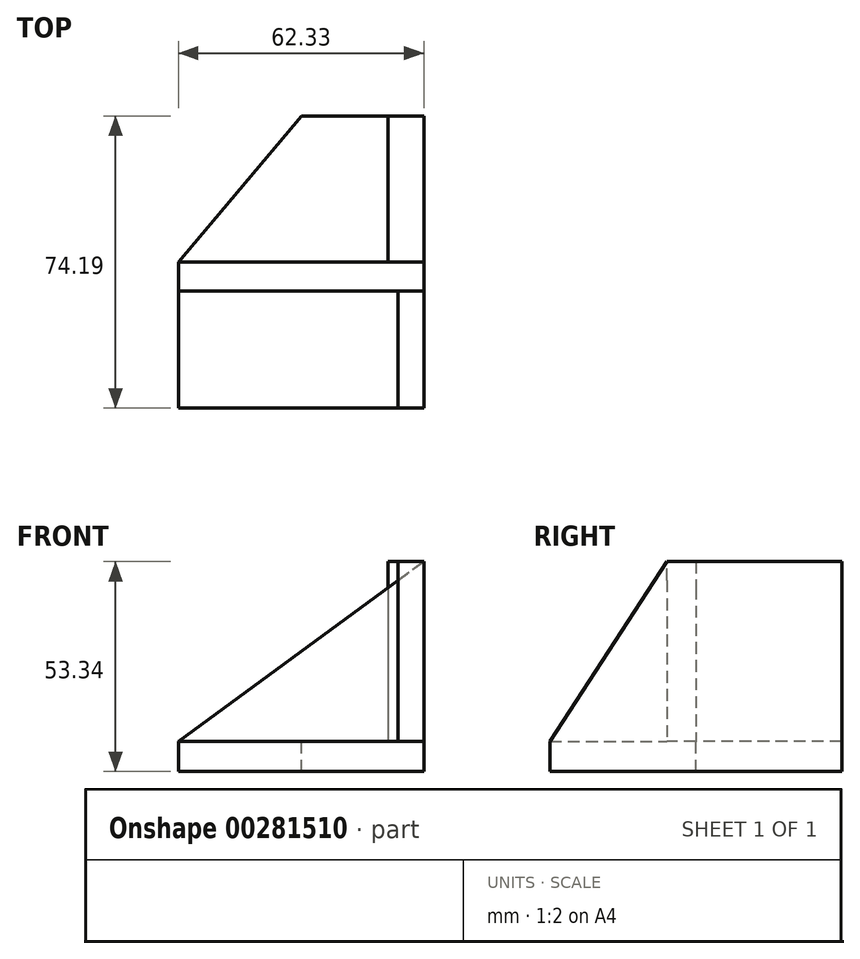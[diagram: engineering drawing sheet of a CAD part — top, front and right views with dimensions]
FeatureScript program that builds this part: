
annotation { "Feature Type Name" : "Feature", "Feature Type Description" : "" }
export const myFeature = defineFeature(function(context is Context, id is Id, definition is map)
    precondition{}
    {
        {
            var Q0;
            Q0=qCreatedBy(makeId("Top.planeOp"),FACE);
            var sketch = newSketch(context, id + "F0", { "sketchPlane" : qUnion([Q0])});
            skLineSegment(sketch, "E0.bottom", {"start": v(-31.28, 35.35) * mm, "end": v(31.05, 35.35) * mm});
            skLineSegment(sketch, "E0.top", {"start": v(-31.28, -38.84) * mm, "end": v(31.05, -38.84) * mm});
            skLineSegment(sketch, "E0.left", {"start": v(-31.28, 35.35) * mm, "end": v(-31.28, -38.84) * mm});
            skLineSegment(sketch, "E0.right", {"start": v(31.05, 35.35) * mm, "end": v(31.05, -38.84) * mm});
            skSolve(sketch);
        }
        {
            var Q0;
            Q0=makeQuery(id+"F0.imprint","IMPRINT",FACE,{"disambiguationData":[TD([[makeQuery(id+"F0.imprint","IMPRINT",EDGE,{"derivedFrom":sQuery(id+"F0.wireOp",EDGE,"E0.bottom")}),-1.0]])]});
            extrude(context, id + "F1", {"entities" : qUnion([Q0]), "depth" : 7.62 * mm});
        }
        {
            var Q0;
            Q0=makeQuery(id+"F1.opExtrude","CAP_FACE",FACE,{"disambiguationData":[OSD([sQuery(id+"F0.wireOp",EDGE,"E0.bottom"),sQuery(id+"F0.wireOp",EDGE,"E0.top"),sQuery(id+"F0.wireOp",EDGE,"E0.left"),sQuery(id+"F0.wireOp",EDGE,"E0.right")])],"isStart":false});
            var sketch = newSketch(context, id + "F2", { "sketchPlane" : qUnion([Q0])});
            skLineSegment(sketch, "E1", {"start": v(-31.28, -1.74) * mm, "end": v(0, 35.35) * mm});
            skSolve(sketch);
        }
        {
            var Q0;
            {var subQ0=sQuery(id+"F2.wireOp",EDGE,"E1");Q0=makeQuery(id+"F2.imprint","IMPRINT",FACE,{"disambiguationData":[TD([[makeQuery(id+"F2.imprint","IMPRINT",EDGE,{"derivedFrom":subQ0}),1.0]])]});}
            extrude(context, id + "F3", {"entities" : qUnion([Q0]), "operationType" : NewBodyOperationType.ADD, "depth" : 25.4 * mm});
        }
        {
            var Q0;
            Q0=makeQuery(id+"F3.opExtrude","CAP_FACE",FACE,{"disambiguationData":[OSD([sQuery(id+"F0.wireOp",EDGE,"E0.bottom"),sQuery(id+"F0.wireOp",EDGE,"E0.left"),sQuery(id+"F2.wireOp",EDGE,"E1")])],"isStart":false});
            extrude(context, id + "F4", {"entities" : qUnion([Q0]), "operationType" : NewBodyOperationType.REMOVE, "oppositeDirection" : true, "depth" : 33.02 * mm});
        }
        {
            var Q0;
            Q0=makeQuery(id+"F1.opExtrude","CAP_FACE",FACE,{"disambiguationData":[OSD([sQuery(id+"F0.wireOp",EDGE,"E0.bottom"),sQuery(id+"F0.wireOp",EDGE,"E0.top"),sQuery(id+"F0.wireOp",EDGE,"E0.left"),sQuery(id+"F0.wireOp",EDGE,"E0.right")])],"isStart":false});
            var sketch = newSketch(context, id + "F5", { "sketchPlane" : qUnion([Q0])});
            skLineSegment(sketch, "E2.bottom", {"start": v(-31.28, -1.74) * mm, "end": v(31.05, -1.74) * mm});
            skLineSegment(sketch, "E2.top", {"start": v(-31.28, -9.07) * mm, "end": v(31.05, -9.07) * mm});
            skLineSegment(sketch, "E2.left", {"start": v(-31.28, -1.74) * mm, "end": v(-31.28, -9.07) * mm});
            skLineSegment(sketch, "E2.right", {"start": v(31.05, -1.74) * mm, "end": v(31.05, -9.07) * mm});
            skSolve(sketch);
        }
        {
            var Q0;
            Q0=makeQuery(id+"F5.imprint","IMPRINT",FACE,{"disambiguationData":[TD([[makeQuery(id+"F5.imprint","IMPRINT",EDGE,{"derivedFrom":sQuery(id+"F5.wireOp",EDGE,"E2.bottom")}),-1.0]])]});
            extrude(context, id + "F6", {"entities" : qUnion([Q0]), "operationType" : NewBodyOperationType.ADD, "depth" : 45.72 * mm});
        }
        {
            var Q0;
            Q0=makeQuery(id+"F6.opExtrude","SWEPT_FACE",FACE,{"disambiguationData":[OSD([sQuery(id+"F5.wireOp",EDGE,"E2.top")])]});
            var sketch = newSketch(context, id + "F7", { "sketchPlane" : qUnion([Q0])});
            skLineSegment(sketch, "E3", {"start": v(-31.28, 7.62) * mm, "end": v(31.05, 53.34) * mm});
            skSolve(sketch);
        }
        {
            var Q0;
            Q0=makeQuery(id+"F7.imprint","IMPRINT",FACE,{"disambiguationData":[TD([[makeQuery(id+"F7.imprint","IMPRINT",EDGE,{"derivedFrom":sQuery(id+"F7.wireOp",EDGE,"E3")}),1.0]])]});
            extrude(context, id + "F8", {"entities" : qUnion([Q0]), "operationType" : NewBodyOperationType.REMOVE, "oppositeDirection" : true, "depth" : 25.4 * mm});
        }
        {
            var Q0;
            {var subQ0=sQuery(id+"F0.wireOp",EDGE,"E0.left");var subQ1=sQuery(id+"F0.wireOp",EDGE,"E0.right");var subQ2=sQuery(id+"F0.wireOp",EDGE,"E0.top");Q0=makeQuery(id+"F6.boolean.opBoolean","SPLIT",FACE,{"disambiguationData":[TD([makeQuery(id+"F1.opExtrude","SWEPT_FACE",FACE,{"disambiguationData":[OSD([subQ2])]})])],"derivedFrom":makeQuery(id+"F1.opExtrude","CAP_FACE",FACE,{"disambiguationData":[OSD([sQuery(id+"F0.wireOp",EDGE,"E0.bottom"),subQ2,subQ0,subQ1])],"isStart":false})});}
            var sketch = newSketch(context, id + "F9", { "sketchPlane" : qUnion([Q0])});
            skLineSegment(sketch, "E4.bottom", {"start": v(31.05, -38.84) * mm, "end": v(24.54, -38.84) * mm});
            skLineSegment(sketch, "E4.top", {"start": v(31.05, -9.07) * mm, "end": v(24.54, -9.07) * mm});
            skLineSegment(sketch, "E4.left", {"start": v(31.05, -38.84) * mm, "end": v(31.05, -9.07) * mm});
            skLineSegment(sketch, "E4.right", {"start": v(24.54, -38.84) * mm, "end": v(24.54, -9.07) * mm});
            skSolve(sketch);
        }
        {
            var Q0;
            Q0=makeQuery(id+"F9.imprint","IMPRINT",FACE,{"disambiguationData":[TD([[makeQuery(id+"F9.imprint","IMPRINT",EDGE,{"derivedFrom":sQuery(id+"F9.wireOp",EDGE,"E4.bottom")}),1.0]])]});
            extrude(context, id + "F10", {"entities" : qUnion([Q0]), "operationType" : NewBodyOperationType.ADD, "depth" : 45.72 * mm});
        }
        {
            var Q0;
            Q0=makeQuery(id+"F10.opExtrude","SWEPT_FACE",FACE,{"disambiguationData":[OSD([sQuery(id+"F9.wireOp",EDGE,"E4.right")])]});
            var sketch = newSketch(context, id + "F11", { "sketchPlane" : qUnion([Q0])});
            skLineSegment(sketch, "E5", {"start": v(9.07, 53.34) * mm, "end": v(38.84, 7.62) * mm});
            skSolve(sketch);
        }
        {
            var Q0;
            Q0=makeQuery(id+"F11.imprint","IMPRINT",FACE,{"disambiguationData":[TD([[makeQuery(id+"F11.imprint","IMPRINT",EDGE,{"derivedFrom":sQuery(id+"F11.wireOp",EDGE,"E5")}),1.0]])]});
            extrude(context, id + "F12", {"entities" : qUnion([Q0]), "operationType" : NewBodyOperationType.REMOVE, "oppositeDirection" : true, "depth" : 25.4 * mm});
        }
        {
            var Q0;
            {var subQ0=sQuery(id+"F0.wireOp",EDGE,"E0.right");var subQ1=sQuery(id+"F0.wireOp",EDGE,"E0.left");var subQ2=sQuery(id+"F0.wireOp",EDGE,"E0.bottom");Q0=makeQuery(id+"F6.boolean.opBoolean","SPLIT",FACE,{"disambiguationData":[TD([makeQuery(id+"F1.opExtrude","SWEPT_FACE",FACE,{"disambiguationData":[OSD([subQ2])]})])],"derivedFrom":makeQuery(id+"F1.opExtrude","CAP_FACE",FACE,{"disambiguationData":[OSD([subQ2,sQuery(id+"F0.wireOp",EDGE,"E0.top"),subQ1,subQ0])],"isStart":false})});}
            var sketch = newSketch(context, id + "F13", { "sketchPlane" : qUnion([Q0])});
            skLineSegment(sketch, "E6.bottom", {"start": v(31.05, 35.35) * mm, "end": v(21.98, 35.35) * mm});
            skLineSegment(sketch, "E6.top", {"start": v(31.05, -1.74) * mm, "end": v(21.98, -1.74) * mm});
            skLineSegment(sketch, "E6.left", {"start": v(31.05, 35.35) * mm, "end": v(31.05, -1.74) * mm});
            skLineSegment(sketch, "E6.right", {"start": v(21.98, 35.35) * mm, "end": v(21.98, -1.74) * mm});
            skSolve(sketch);
        }
        {
            var Q0;
            Q0=makeQuery(id+"F13.imprint","IMPRINT",FACE,{"disambiguationData":[TD([[makeQuery(id+"F13.imprint","IMPRINT",EDGE,{"derivedFrom":sQuery(id+"F13.wireOp",EDGE,"E6.bottom")}),-1.0]])]});
            extrude(context, id + "F14", {"entities" : qUnion([Q0]), "operationType" : NewBodyOperationType.ADD, "depth" : 45.72 * mm});
        }
    });
